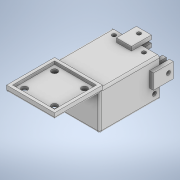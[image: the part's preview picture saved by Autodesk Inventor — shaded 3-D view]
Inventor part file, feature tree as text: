
AUTODESK INVENTOR PART (.ipt)
format: ipt  version: 2020 (Build 240168000, 168)  size: 347,136 bytes
history: native  units: in
note: dims shown in document units (in); Inventor stores cm internally (conversion verified against a paired STEP export)
features: extrude x17, sketch x17, mirror x3, fillet x1
ambient origin geometry x8: Origin, YZ Plane, XZ Plane, XY Plane, X Axis, Y Axis, Z Axis, Center Point
bodies: Solid1 (feature_tree)
feature tree (38):
  extrude  "Extrusion1"  Depth=1.8898in
  extrude  "Extrusion2"  Depth=0.1181in
  mirror  "Mirror1"
  extrude  "Extrusion3"  Depth=0.1181in
  extrude  "Extrusion4"  Depth=0.1181in
  extrude  "Extrusion5"  Depth=0.1181in
  extrude  "Extrusion6"  Depth=0.1181in
  mirror  "Mirror2"
  extrude  "Extrusion7"  Depth=0.1575in
  mirror  "Mirror3"
  extrude  "Extrusion8"  Depth=0.1575in
  extrude  "Extrusion9"  Depth=0.1575in
  extrude  "Extrusion10"  Depth=0.2362in
  extrude  "Extrusion11"  Depth=0.2362in
  extrude  "Extrusion12"  Depth=0.1575in TaperAngle=0.0deg
  extrude  "Extrusion13"  Depth=0.1181in TaperAngle=0.0deg
  extrude  "Extrusion14"  Depth=0.315in
  extrude  "Extrusion15"  Depth=0.315in
  extrude  "Extrusion16"  Depth=0.2362in
  extrude  "Extrusion17"  Depth=0.2362in
  fillet  "Fillet1"  Radius=0.2362in
  sketch  "Sketch1"  dims[d0=1.8898in d1=10.8661in]
  sketch  "Sketch2"  dims[d2=0.1181in d3=0.0in d4=0.1181in]
  sketch  "Sketch3"  dims[d5=1.8898in d6=0.1181in]
  sketch  "Sketch4"  dims[d7=0.1181in d8=0.1181in]
  sketch  "Sketch5"  dims[d9=0.1181in d10=0.0in d11=0.1181in]
  sketch  "Sketch6"  dims[d12=0.1181in d13=0.1181in]
  sketch  "Sketch7"  dims[d14=1.378in d15=0.0in d16=0.1575in]
  sketch  "Sketch8"  dims[d17=0.315in d18=0.0in d19=0.1575in]
  sketch  "Sketch9"  dims[d20=0.1575in d21=0.0in d22=0.1575in]
  sketch  "Sketch10"  dims[d23=0.1575in d24=0.0in d25=0.2362in]
  sketch  "Sketch11"  dims[d26=0.2362in d27=0.2362in]
  sketch  "Sketch12"  dims[d28=0.2362in d29=0.1575in d30=0.0in]
  sketch  "Sketch13"  dims[d31=0.1181in d32=1.6654in d33=0.0in]
  sketch  "Sketch14"  dims[d34=0.315in d35=0.315in]
  sketch  "Sketch15"  dims[d36=0.315in d37=0.315in]
  sketch  "Sketch16"  dims[d38=0.1181in d39=0.0in d40=0.2362in]
  sketch  "Sketch17"  dims[d41=0.2362in d42=0.2362in d43=0.2362in d44=0.0787in d45=0.0in d46=0.9843in d47=0.1575in d48=0.1575in d49=0.1575in d50=0.1575in d51=0.3937in d52=0.0in d53=3.937in d54=0.0in d55=0.5906in d56=0.7874in d57=0.1575in d58=0.2756in d59=0.0in d60=0.0in d61=0.7874in d62=0.5906in d63=0.1575in d64=0.2756in d65=0.0in d66=0.0in d67=0.1575in d68=0.1575in d69=0.7874in d70=0.0in d71=0.1575in d72=0.1575in d73=0.1575in d74=0.7874in d75=0.0in d76=0.1181in d77=0.3937in d78=0.0in d79=0.0787in]
